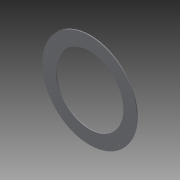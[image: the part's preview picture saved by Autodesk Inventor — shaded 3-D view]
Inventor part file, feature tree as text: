
AUTODESK INVENTOR PART (.ipt)
format: ipt  version: 2013 (Build 170138000, 138)  size: 99,840 bytes
history: native  units: in
note: dims shown in document units (in); Inventor stores cm internally (conversion verified against a paired STEP export)
features: extrude x1, sketch x1
ambient origin geometry x8: Origin, YZ Plane, XZ Plane, XY Plane, X Axis, Y Axis, Z Axis, Center Point
bodies: Solid1 (feature_tree)
feature tree (2):
  extrude  "Extrusion1"  Depth=20.0in
  sketch  "Sketch1"  dims[d0=28.0in d1=20.0in d3=0.25in d4=6.6929in d6=360.0deg d8=0.25in d9=0.0in]
